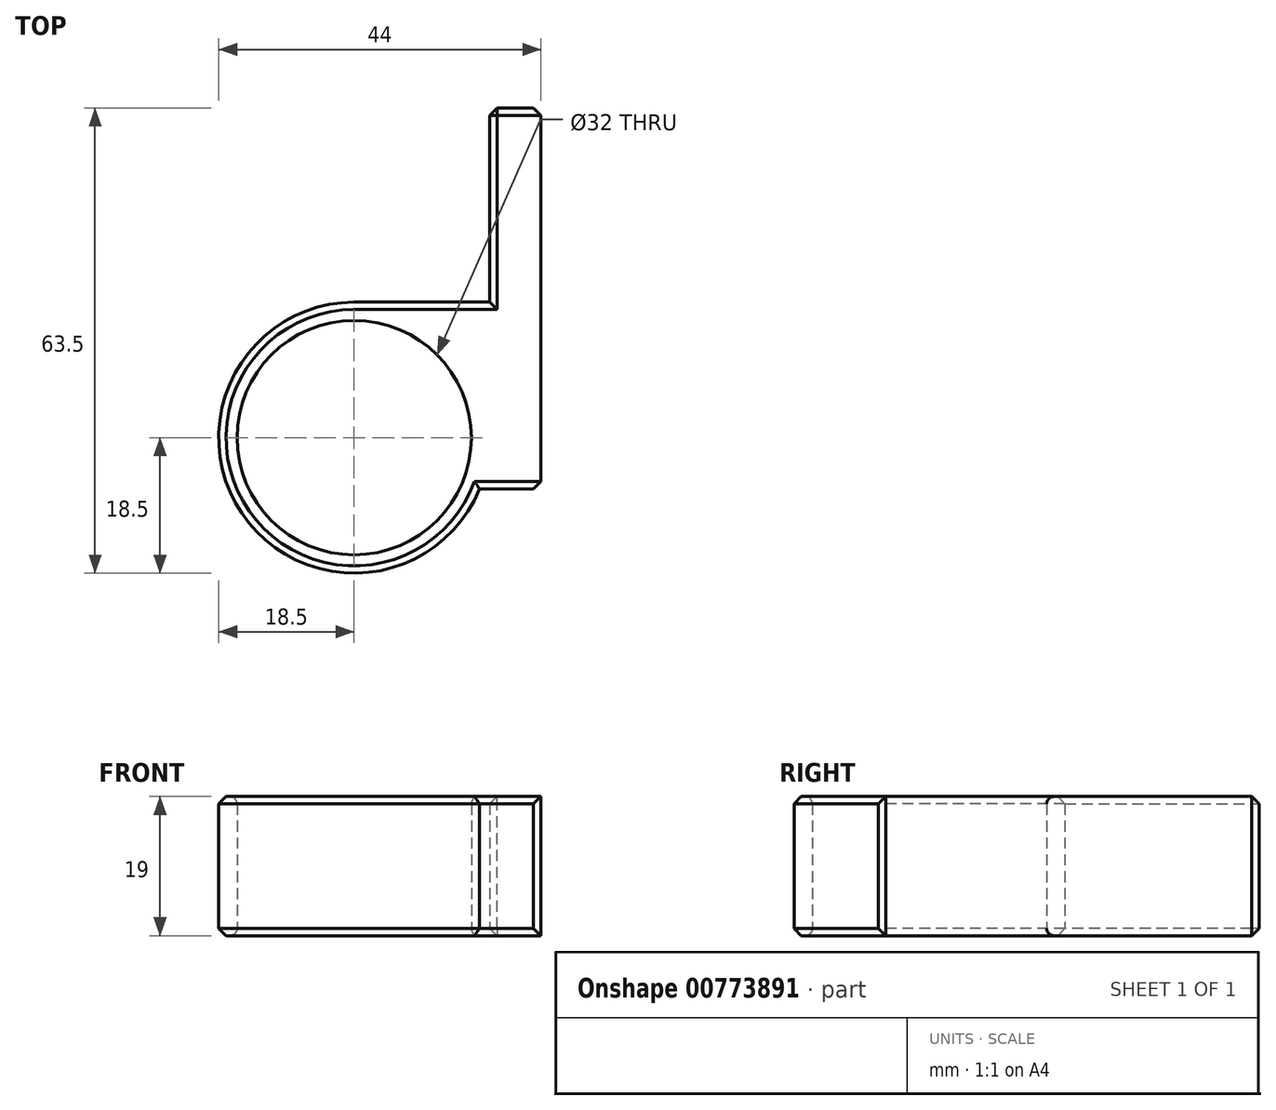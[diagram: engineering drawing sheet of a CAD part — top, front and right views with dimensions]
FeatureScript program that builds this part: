
annotation { "Feature Type Name" : "Feature", "Feature Type Description" : "" }
export const myFeature = defineFeature(function(context is Context, id is Id, definition is map)
    precondition{}
    {
        {
            assignVariable(context, id + "F0", {"name" : "Width", "anyValue" : 19});
        }
        {
            var Q0;
            Q0=qCreatedBy(makeId("Top.planeOp"),FACE);
            var sketch = newSketch(context, id + "F1", { "sketchPlane" : qUnion([Q0])});
            skCircle(sketch, "E0", {"center": v(0, 0) * mm, "radius": 16 * mm});
            skCircle(sketch, "E1", {"center": v(0, 0) * mm, "radius": 18.5 * mm});
            skLineSegment(sketch, "E2.bottom", {"start": v(18.5, 0) * mm, "end": v(25.5, 0) * mm});
            skLineSegment(sketch, "E2.top", {"start": v(18.5, 45) * mm, "end": v(25.5, 45) * mm});
            skLineSegment(sketch, "E2.left", {"start": v(18.5, 0) * mm, "end": v(18.5, 45) * mm});
            skLineSegment(sketch, "E2.right", {"start": v(25.5, 0) * mm, "end": v(25.5, 45) * mm});
            skLineSegment(sketch, "E3.top", {"start": v(18.5, -7) * mm, "end": v(25.5, -7) * mm});
            skLineSegment(sketch, "E3.left", {"start": v(18.5, 0) * mm, "end": v(18.5, -7) * mm});
            skLineSegment(sketch, "E3.right", {"start": v(25.5, 0) * mm, "end": v(25.5, -7) * mm});
            skLineSegment(sketch, "E4", {"start": v(18.5, -7) * mm, "end": v(17.12, -7) * mm});
            skLineSegment(sketch, "E5", {"start": v(0, 18.5) * mm, "end": v(18.5, 18.5) * mm});
            skSolve(sketch);
        }
        {
            var Q0;
            Q0=makeQuery(id+"F1.imprint","IMPRINT",FACE,{"disambiguationData":[TD([[makeQuery(id+"F1.imprint","IMPRINT",EDGE,{"derivedFrom":sQuery(id+"F1.wireOp",EDGE,"E0")}),-1.0]])]});
            var Q1;
            {var subQ3=sQuery(id+"F1.wireOp",EDGE,"E5");Q1=makeQuery(id+"F1.imprint","IMPRINT",FACE,{"disambiguationData":[TD([[makeQuery(id+"F1.imprint","IMPRINT",EDGE,{"derivedFrom":subQ3}),-1.0]])]});}
            var Q2;
            {var subQ1=sQuery(id+"F1.wireOp",EDGE,"E2.top");Q2=makeQuery(id+"F1.imprint","IMPRINT",FACE,{"disambiguationData":[TD([[makeQuery(id+"F1.imprint","IMPRINT",EDGE,{"derivedFrom":subQ1}),-1.0]])]});}
            var Q3;
            {var subQ0=sQuery(id+"F1.wireOp",EDGE,"E3.left");Q3=makeQuery(id+"F1.imprint","IMPRINT",FACE,{"disambiguationData":[TD([[makeQuery(id+"F1.imprint","IMPRINT",EDGE,{"derivedFrom":subQ0}),-1.0]])]});}
            var Q4;
            Q4=makeQuery(id+"F1.imprint","IMPRINT",FACE,{"disambiguationData":[TD([[makeQuery(id+"F1.imprint","IMPRINT",EDGE,{"derivedFrom":sQuery(id+"F1.wireOp",EDGE,"E2.bottom")}),-1.0]])]});
            extrude(context, id + "F2", {"entities" : qUnion([Q0, Q1, Q2, Q3, Q4]), "depth" : getVariable(context, 'Width') * mm, "offsetDistance" : 25 * mm});
        }
        {
            var Q0;
            Q0=makeQuery(id+"F2.opExtrude","SWEPT_EDGE",EDGE,{"disambiguationData":[OSD([sQuery(id+"F1.wireOp",EDGE,"E3.top"),sQuery(id+"F1.wireOp",EDGE,"E3.right")])]});
            chamfer(context, id + "F3", {"entities" : qUnion([Q0]), "width" : 1 * mm, "tangentPropagation" : true});
        }
        {
            var Q0;
            Q0=makeQuery(id+"F2.opExtrude","CAP_EDGE",EDGE,{"disambiguationData":[OSD([sQuery(id+"F1.wireOp",EDGE,"E0")])],"isStart":false});
            var Q1;
            Q1=makeQuery(id+"F2.opExtrude","CAP_EDGE",EDGE,{"disambiguationData":[OSD([sQuery(id+"F1.wireOp",EDGE,"E0")])],"isStart":true});
            fillet(context, id + "F4", {"entities" : qUnion([Q0, Q1]), "radius" : 1 * mm, "tangentPropagation" : true, "allowEdgeOverflow" : false});
        }
        {
            var Q0;
            Q0=makeQuery(id+"F2.opExtrude","CAP_EDGE",EDGE,{"disambiguationData":[OSD([sQuery(id+"F1.wireOp",EDGE,"E5")])],"isStart":false});
            var Q1;
            Q1=makeQuery(id+"F2.opExtrude","CAP_EDGE",EDGE,{"disambiguationData":[OSD([sQuery(id+"F1.wireOp",EDGE,"E1")])],"isStart":false});
            var Q2;
            Q2=makeQuery(id+"F2.opExtrude","CAP_EDGE",EDGE,{"disambiguationData":[OSD([sQuery(id+"F1.wireOp",EDGE,"E1")])],"isStart":true});
            var Q3;
            Q3=makeQuery(id+"F2.opExtrude","CAP_EDGE",EDGE,{"disambiguationData":[OSD([sQuery(id+"F1.wireOp",EDGE,"E5")])],"isStart":true});
            chamfer(context, id + "F5", {"entities" : qUnion([Q0, Q1, Q2, Q3]), "width" : 1 * mm, "tangentPropagation" : true});
        }
        {
            var Q0;
            Q0=makeQuery(id+"F2.opExtrude","SWEPT_EDGE",EDGE,{"disambiguationData":[OSD([sQuery(id+"F1.wireOp",EDGE,"E2.top"),sQuery(id+"F1.wireOp",EDGE,"E2.left")])]});
            var Q1;
            Q1=makeQuery(id+"F2.opExtrude","CAP_EDGE",EDGE,{"disambiguationData":[OSD([sQuery(id+"F1.wireOp",EDGE,"E2.top")])],"isStart":true});
            var Q2;
            Q2=makeQuery(id+"F2.opExtrude","CAP_EDGE",EDGE,{"disambiguationData":[OSD([sQuery(id+"F1.wireOp",EDGE,"E2.top")])],"isStart":false});
            var Q3;
            Q3=makeQuery(id+"F2.opExtrude","SWEPT_EDGE",EDGE,{"disambiguationData":[OSD([sQuery(id+"F1.wireOp",EDGE,"E2.top"),sQuery(id+"F1.wireOp",EDGE,"E2.right")])]});
            var Q4;
            Q4=makeQuery(id+"F2.opExtrude","CAP_EDGE",EDGE,{"disambiguationData":[OSD([sQuery(id+"F1.wireOp",EDGE,"E2.left")])],"isStart":false});
            var Q5;
            Q5=makeQuery(id+"F2.opExtrude","CAP_EDGE",EDGE,{"disambiguationData":[OSD([sQuery(id+"F1.wireOp",EDGE,"E2.left")])],"isStart":true});
            var Q6;
            Q6=makeQuery(id+"F2.opExtrude","CAP_EDGE",EDGE,{"disambiguationData":[OSD([sQuery(id+"F1.wireOp",EDGE,"E3.top"),sQuery(id+"F1.wireOp",EDGE,"E4")])],"isStart":false});
            var Q7;
            Q7=makeQuery(id+"F2.opExtrude","CAP_EDGE",EDGE,{"disambiguationData":[OSD([sQuery(id+"F1.wireOp",EDGE,"E3.top"),sQuery(id+"F1.wireOp",EDGE,"E4")])],"isStart":true});
            chamfer(context, id + "F6", {"entities" : qUnion([Q0, Q1, Q2, Q3, Q4, Q5, Q6, Q7]), "width" : 1 * mm, "tangentPropagation" : true});
        }
    });
